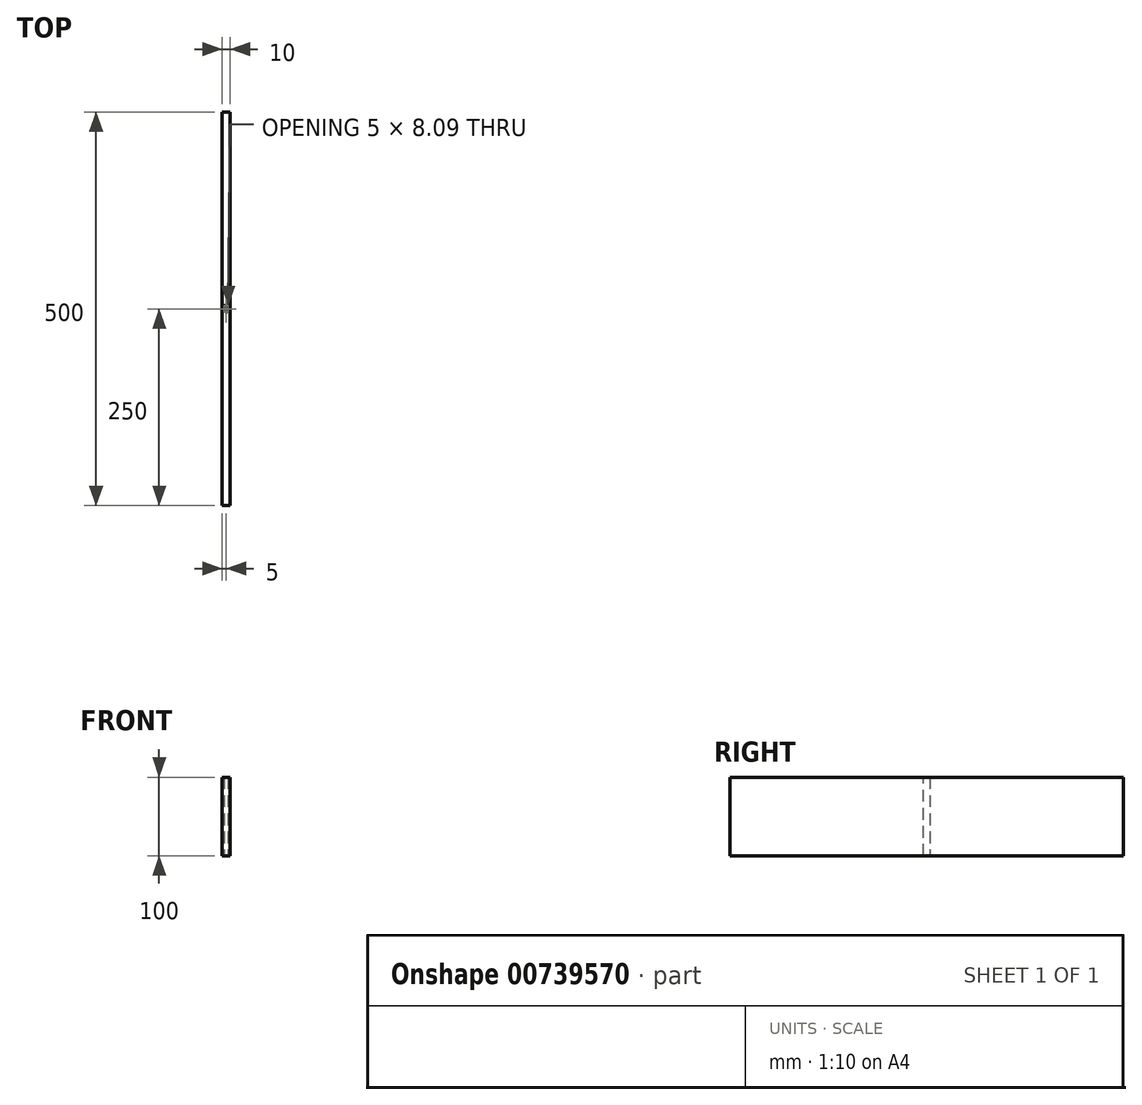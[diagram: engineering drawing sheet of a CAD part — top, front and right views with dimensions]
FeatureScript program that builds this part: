
annotation { "Feature Type Name" : "Feature", "Feature Type Description" : "" }
export const myFeature = defineFeature(function(context is Context, id is Id, definition is map)
    precondition{}
    {
        {
            assignVariable(context, id + "F0", {"name" : "h", "anyValue" : 100 * mm});
        }
        {
            var Q0;
            Q0=qCreatedBy(makeId("Top.planeOp"),FACE);
            var sketch = newSketch(context, id + "F1", { "sketchPlane" : qUnion([Q0])});
            skLineSegment(sketch, "E0.bottom", {"start": v(5, 250) * mm, "end": v(-5, 250) * mm});
            skLineSegment(sketch, "E0.top", {"start": v(5, -250) * mm, "end": v(-5, -250) * mm});
            skLineSegment(sketch, "E0.left", {"start": v(5, 250) * mm, "end": v(5, -250) * mm});
            skLineSegment(sketch, "E0.right", {"start": v(-5, 250) * mm, "end": v(-5, -250) * mm});
            skPoint(sketch, "E0.middle", {"position": v(0, 0) * mm});
            skLineSegment(sketch, "E1", {"start": v(0, 250) * mm, "end": v(0, -250) * mm});
            skEllipse(sketch, "E2", {"center": v(5, 0) * mm, "majorRadius": 4.04 * mm, "minorRadius": 2.5 * mm, "majorAxis": v(0, 1)});
            skLineSegment(sketch, "E3", {"start": v(2.5, 0) * mm, "end": v(2.5, -4.04) * mm});
            skLineSegment(sketch, "E4", {"start": v(5, -4.04) * mm, "end": v(2.5, -4.04) * mm});
            skPoint(sketch, "E5", {"position": v(7.5, 0) * mm});
            skPoint(sketch, "E6", {"position": v(5, 4.05) * mm});
            skSolve(sketch);
        }
        {
            var Q0;
            {var subQ8=sQuery(id+"F1.wireOp",EDGE,"E1");Q0=makeQuery(id+"F1.imprint","IMPRINT",FACE,{"disambiguationData":[TD([[makeQuery(id+"F1.imprint","IMPRINT",EDGE,{"derivedFrom":subQ8}),1.0]])]});}
            extrude(context, id + "F2", {"entities" : qUnion([Q0]), "depth" : getVariable(context, 'h'), "offsetDistance" : 25 * mm});
        }
        {
            var Q0;
            Q0=sQuery(id+"F1.wireOp",EDGE,"E0.left");
            cPoint(context, id + "F3", {"entities" : qUnion([Q0]), "parameter" : 0.5});
        }
        {
            var Q0;
            Q0=makeQuery(id+"F2.opExtrude","SWEPT_BODY",BODY,{"disambiguationData":[OSD([sQuery(id+"F1.wireOp",EDGE,"E0.bottom"),sQuery(id+"F1.wireOp",EDGE,"E0.top"),sQuery(id+"F1.wireOp",EDGE,"E0.left"),sQuery(id+"F1.wireOp",EDGE,"E1"),sQuery(id+"F1.wireOp",EDGE,"E2"),sQuery(id+"F1.wireOp",EDGE,"E3"),sQuery(id+"F1.wireOp",EDGE,"E4")])]});
            var Q1;
            Q1=qCreatedBy(id+"F3",VERTEX);
            var Q2;
            Q2=sQuery(id+"F1.wireOp",VERTEX,"E0.middle");
            transform(context, id + "F4", {"entities" : qUnion([Q0]), "transformType" : TransformType.TRANSLATION_ENTITY, "oppositeDirectionEntity" : false, "transformLine" : qUnion([Q1, Q2]), "makeCopy" : false});
        }
        {
            var Q0;
            Q0=makeQuery(id+"F2.opExtrude","SWEPT_BODY",BODY,{"disambiguationData":[OSD([sQuery(id+"F1.wireOp",EDGE,"E0.bottom"),sQuery(id+"F1.wireOp",EDGE,"E0.top"),sQuery(id+"F1.wireOp",EDGE,"E0.left"),sQuery(id+"F1.wireOp",EDGE,"E1"),sQuery(id+"F1.wireOp",EDGE,"E2"),sQuery(id+"F1.wireOp",EDGE,"E3"),sQuery(id+"F1.wireOp",EDGE,"E4")])]});
            var Q1;
            Q1=qCreatedBy(makeId("Right.planeOp"),FACE);
            mirror(context, id + "F5", {"operationType" : NewBodyOperationType.ADD, "entities" : qUnion([Q0]), "mirrorPlane" : qUnion([Q1])});
        }
        {
            var Q0;
            Q0=makeQuery(id+"F2.opExtrude","SWEPT_BODY",BODY,{"disambiguationData":[OSD([sQuery(id+"F1.wireOp",EDGE,"E0.bottom"),sQuery(id+"F1.wireOp",EDGE,"E0.top"),sQuery(id+"F1.wireOp",EDGE,"E0.left"),sQuery(id+"F1.wireOp",EDGE,"E1"),sQuery(id+"F1.wireOp",EDGE,"E2"),sQuery(id+"F1.wireOp",EDGE,"E3"),sQuery(id+"F1.wireOp",EDGE,"E4")])]});
            var Q1;
            Q1=makeQuery(id+"F5.opPattern","COPY",EDGE,{"derivedFrom":makeQuery(id+"F2.opExtrude","SWEPT_EDGE",EDGE,{"disambiguationData":[OSD([sQuery(id+"F1.wireOp",EDGE,"E0.top"),sQuery(id+"F1.wireOp",EDGE,"E1")])]}),"instanceName":"1"});
            transform(context, id + "F6", {"entities" : qUnion([Q0]), "transformType" : TransformType.ROTATION, "transformAxis" : qUnion([Q1]), "angle" : 180 * degree, "makeCopy" : false});
        }
        {
            var Q0;
            {var subQ0=makeQuery(id+"F2.opExtrude","CAP_FACE",FACE,{"disambiguationData":[OSD([sQuery(id+"F1.wireOp",EDGE,"E0.bottom"),sQuery(id+"F1.wireOp",EDGE,"E0.top"),sQuery(id+"F1.wireOp",EDGE,"E0.left"),sQuery(id+"F1.wireOp",EDGE,"E1"),sQuery(id+"F1.wireOp",EDGE,"E2"),sQuery(id+"F1.wireOp",EDGE,"E3"),sQuery(id+"F1.wireOp",EDGE,"E4")])],"isStart":true});Q0=makeQuery(id+"F5.boolean.opBoolean","MERGE",FACE,{"derivedFrom":[subQ0,makeQuery(id+"F5.opPattern","COPY",FACE,{"derivedFrom":subQ0,"instanceName":"1"})]});}
            var sketch = newSketch(context, id + "F7", { "sketchPlane" : qUnion([Q0])});
            skLineSegment(sketch, "E7", {"start": v(12.5, 500) * mm, "end": v(7.5, 500) * mm});
            skLineSegment(sketch, "E8", {"start": v(10, 495.95) * mm, "end": v(10, 504.04) * mm});
            skPoint(sketch, "E9", {"position": v(10, 500) * mm});
            skSolve(sketch);
        }
        {
            var Q0;
            Q0=sQuery(id+"F7.wireOp",EDGE,"E8");
            cPoint(context, id + "F8", {"entities" : qUnion([Q0]), "parameter" : 0.5});
        }
        {
            var Q0;
            Q0=makeQuery(id+"F2.opExtrude","SWEPT_BODY",BODY,{"disambiguationData":[OSD([sQuery(id+"F1.wireOp",EDGE,"E0.bottom"),sQuery(id+"F1.wireOp",EDGE,"E0.top"),sQuery(id+"F1.wireOp",EDGE,"E0.left"),sQuery(id+"F1.wireOp",EDGE,"E1"),sQuery(id+"F1.wireOp",EDGE,"E2"),sQuery(id+"F1.wireOp",EDGE,"E3"),sQuery(id+"F1.wireOp",EDGE,"E4")])]});
            var Q1;
            Q1 = qCreatedBy(id + "F8" ,VERTEX);
            var Q2;
            Q2=qCreatedBy(makeId("Origin.pointOp"),VERTEX);
            transform(context, id + "F9", {"entities" : qUnion([Q0]), "transformType" : TransformType.TRANSLATION_ENTITY, "oppositeDirectionEntity" : false, "transformLine" : qUnion([Q1, Q2]), "makeCopy" : false});
        }
    });
